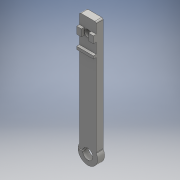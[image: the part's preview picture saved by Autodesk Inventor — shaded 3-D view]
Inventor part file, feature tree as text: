
AUTODESK INVENTOR PART (.ipt)
format: ipt  version: 2016 (Build 200138000, 138)  size: 209,408 bytes
history: native  units: mm
features: sketch x7, extrude x6, projected_geometry x5, fillet x2, hole x1, draft x1
ambient origin geometry x8: Origin, YZ Plane, XZ Plane, XY Plane, X Axis, Y Axis, Z Axis, Center Point
bodies: Solid1 (feature_tree)
feature tree (22):
  extrude  "Extrusion1"  Depth=10.0mm
  hole  "Hole1"  [1 undecoded]
  draft  "FaceDraft1"
  extrude  "Extrusion2"  Depth=10.0mm TaperAngle=0.0deg
  fillet  "Fillet2"  Radius=0.5mm
  extrude  "Extrusion3"  Depth=10.0mm
  extrude  "Extrusion4"  Depth=5.0mm
  extrude  "Extrusion5"  Depth=5.1mm
  extrude  "Extrusion6"  Depth=1.0mm TaperAngle=0.0deg
  fillet  "Fillet4"  Radius=1.0mm
  sketch  "Sketch1"  dims[d3=5.0mm d4=0.0mm d5=10.0mm]
  sketch  "Sketch2"  dims[d6=5.1mm d7=6.0mm d8=4.0mm d9=2.0mm d10=90.0deg d11=8.0mm d12=20.594885mm d14=15.0deg]
  sketch  "Sketch3"  dims[d15=0.6mm d16=10.0mm d17=0.0mm d18=0.5mm]
  sketch  "Sketch4"  dims[d19=10.0mm d21=20.0mm]
  sketch  "Sketch5"  dims[d22=2.0mm d23=5.0mm]
  projected_geometry  "Projected Loop1"
  sketch  "Sketch6"  dims[d24=2.0mm d25=0.0mm d26=5.1mm]
  projected_geometry  "Projected Loop2"
  projected_geometry  "Projected Loop3"
  sketch  "Sketch7"  dims[d27=5.1mm d28=2.0mm d29=0.0mm d32=1.0mm d33=0.0mm d34=1.0mm d35=0.0mm d36=1.0mm]
  projected_geometry  "Projected Loop4"
  projected_geometry  "Projected Loop5"
note: 1 required parameter value undecoded (feature->parameter linkage not recoverable at this tier; creation-order binding heuristic only, values carry confidence <= 0.55)
